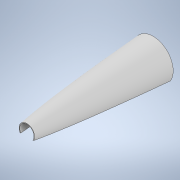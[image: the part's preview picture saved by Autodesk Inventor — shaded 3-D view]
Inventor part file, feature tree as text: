
AUTODESK INVENTOR PART (.ipt)
format: ipt  version: 2020.3 (Build 243373000, 373)  size: 195,072 bytes
history: native  units: mm
features: sketch x1, revolve x1, extrude x1
ambient origin geometry x8: Origin, YZ Plane, XZ Plane, XY Plane, X Axis, Y Axis, Z Axis, Center Point
bodies: Body1 (feature_tree)
feature tree (3):
  sketch  "Sketch3"  dims[d54=25.9mm d55=5.0mm d56=0.9mm d57=2.0mm d58=25.9mm d59=5.0mm d60=0.9mm d61=170.0mm d62=200.0mm d63=25.0mm d64=25.0mm d65=198.2mm d66=25.0mm d67=2.0mm d68=170.0mm d69=5.0mm d70=8.0mm d71=170.0mm d72=15.232132mm d73=360.0deg d74=60.0mm d75=0.0mm d7=0.872665mm d8=0.872665mm d21=0.5mm d22=0.872665mm d23=0.5mm d24=0.872665mm]
  revolve  "Revolution5"  Angle=360.0deg
  extrude  "Extrusion5"  Depth=60.0mm TaperAngle=0.0deg
